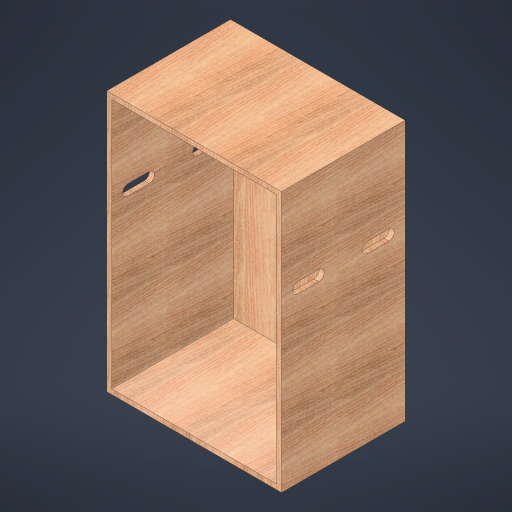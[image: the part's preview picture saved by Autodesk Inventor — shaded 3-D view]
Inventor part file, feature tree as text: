
AUTODESK INVENTOR PART (.ipt)
format: ipt  version: 2023.4 (Build 274418000, 418)  size: 478,208 bytes
history: native  units: in
note: dims shown in document units (in); Inventor stores cm internally (conversion verified against a paired STEP export)
features: extrude x3, sketch x2, projected_geometry x1
ambient origin geometry x8: Origin, YZ Plane, XZ Plane, XY Plane, X Axis, Y Axis, Z Axis, Center Point
bodies: Solid1 (feature_tree)
feature tree (6):
  sketch  "Sketch1"  dims[d0=23.0in d1=35.0in]
  extrude  "Extrusion1"  Depth=35.0in
  extrude  "Extrusion2"  Depth=0.69in
  extrude  "Extrusion3"  Depth=17.0in TaperAngle=0.0deg
  sketch  "Sketch3"  dims[d2=17.25in d3=0.0in d4=0.69in d5=17.0in d6=0.0in d7=4.45in d8=1.48in d9=4.45in d10=1.5in d11=12.0in d12=1.5in d13=0.0in d14=0.0in]
  projected_geometry  "Project Cut Edges1"
